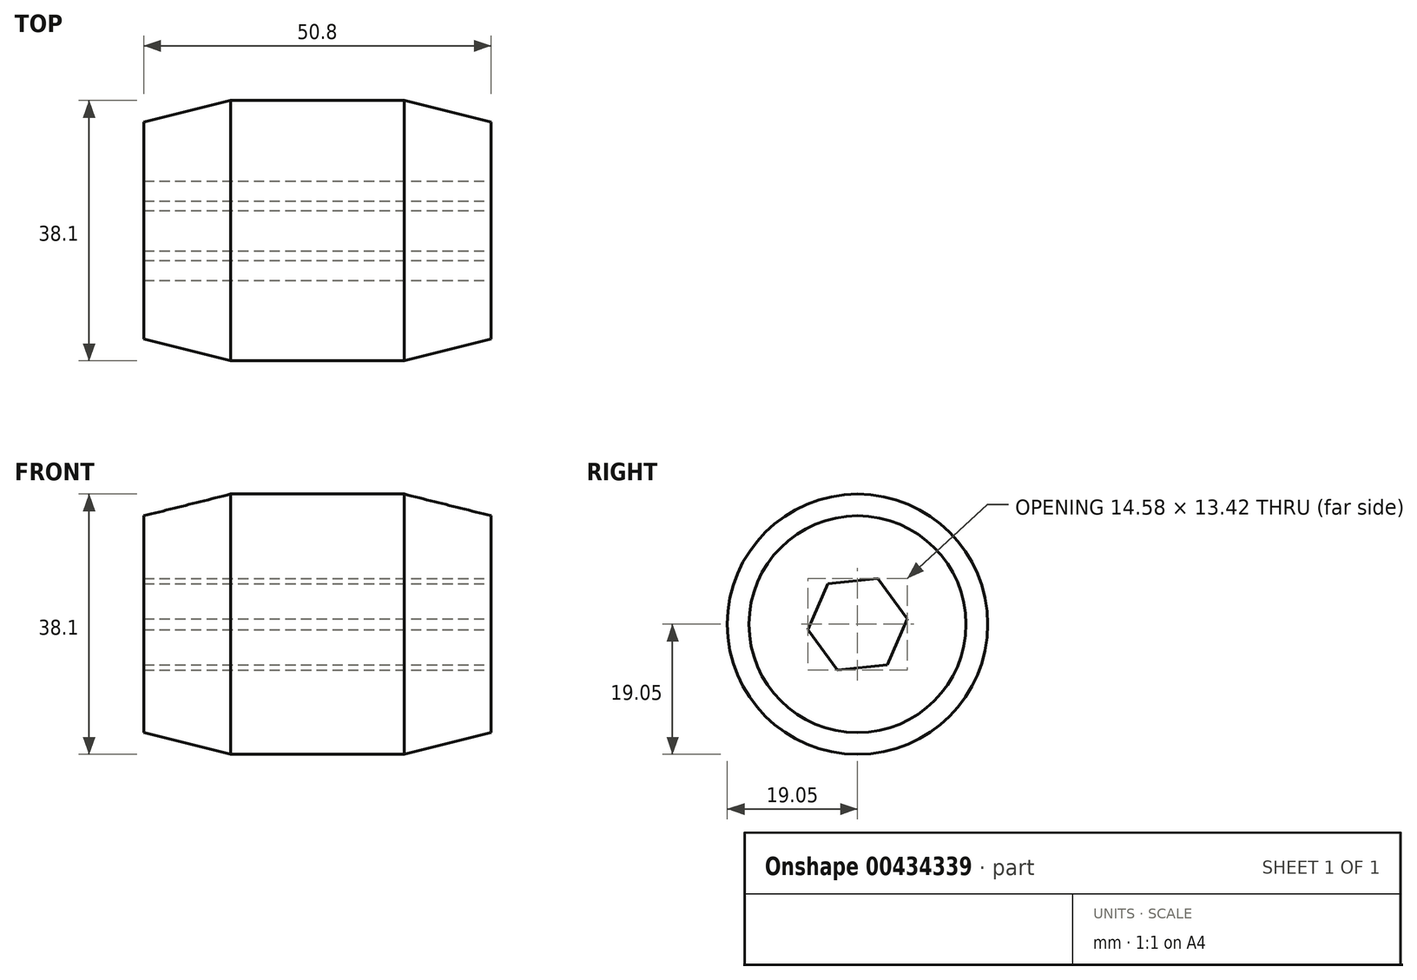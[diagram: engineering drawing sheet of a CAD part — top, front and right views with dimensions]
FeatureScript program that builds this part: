
annotation { "Feature Type Name" : "Feature", "Feature Type Description" : "" }
export const myFeature = defineFeature(function(context is Context, id is Id, definition is map)
    precondition{}
    {
        {
            var Q0;
            Q0=qCreatedBy(makeId("Front.planeOp"),FACE);
            var sketch = newSketch(context, id + "F0", { "sketchPlane" : qUnion([Q0])});
            skLineSegment(sketch, "E0", {"start": v(-41.97, 0) * mm, "end": v(42.8, 0) * mm, "construction": true});
            skLineSegment(sketch, "E1", {"start": v(-24.57, 6.35) * mm, "end": v(26.23, 6.35) * mm});
            skLineSegment(sketch, "E2", {"start": v(-11.87, 19.05) * mm, "end": v(13.53, 19.05) * mm});
            skLineSegment(sketch, "E3", {"start": v(-11.87, 19.05) * mm, "end": v(-24.57, 15.87) * mm});
            skLineSegment(sketch, "E4", {"start": v(13.53, 19.05) * mm, "end": v(26.23, 15.87) * mm});
            skLineSegment(sketch, "E5", {"start": v(26.23, 15.87) * mm, "end": v(26.23, 6.35) * mm});
            skLineSegment(sketch, "E6", {"start": v(-24.57, 15.87) * mm, "end": v(-24.57, 6.35) * mm});
            skSolve(sketch);
        }
        {
            var Q0;
            Q0 = qSketchRegion(id + "F0", true);
            var Q1;
            Q1=sQuery(id+"F0.wireOp",EDGE,"E0");
            revolve(context, id + "F1", {"entities" : qUnion([Q0]), "axis" : qUnion([Q1]), "revolveType" : RevolveType.FULL});
        }
        {
            var Q0;
            Q0=qCreatedBy(makeId("Right.planeOp"),FACE);
            var sketch = newSketch(context, id + "F2", { "sketchPlane" : qUnion([Q0])});
            skCircle(sketch, "E7.cCircle", {"center": v(0, 0) * mm, "radius": 6.35 * mm, "construction": true});
            skLineSegment(sketch, "E7.0", {"start": v(2.96, 6.7) * mm, "end": v(7.29, 0.8) * mm});
            skLineSegment(sketch, "E7.1", {"start": v(7.29, 0.8) * mm, "end": v(4.33, -5.92) * mm});
            skLineSegment(sketch, "E7.2", {"start": v(4.33, -5.92) * mm, "end": v(-2.96, -6.7) * mm});
            skLineSegment(sketch, "E7.3", {"start": v(-2.96, -6.7) * mm, "end": v(-7.29, -0.8) * mm});
            skLineSegment(sketch, "E7.4", {"start": v(-7.29, -0.8) * mm, "end": v(-4.33, 5.92) * mm});
            skLineSegment(sketch, "E7.5", {"start": v(-4.33, 5.92) * mm, "end": v(2.96, 6.7) * mm});
            skPoint(sketch, "E7.0.midPoint", {"position": v(5.12, 3.75) * mm});
            skSolve(sketch);
        }
        {
            var Q0;
            Q0 = qSketchRegion(id + "F2", true);
            extrude(context, id + "F3", {"entities" : qUnion([Q0]), "operationType" : NewBodyOperationType.REMOVE, "oppositeDirection" : true, "depth" : 50.8 * mm, "hasSecondDirection" : true, "secondDirectionOppositeDirection" : true, "secondDirectionDepth" : -50.8 * mm});
        }
    });
